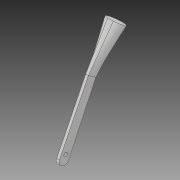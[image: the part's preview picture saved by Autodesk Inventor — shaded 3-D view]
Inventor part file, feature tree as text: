
AUTODESK INVENTOR PART (.ipt)
format: ipt  version: 2017 (Build 210142000, 142)  size: 156,160 bytes
history: native  units: mm
features: thicken_offset x4, sketch x3, extrude x1, fillet x1, plane x1, loft x1, other x1
ambient origin geometry x8: Origin, YZ Plane, XZ Plane, XY Plane, X Axis, Y Axis, Z Axis, Center Point
bodies: Solid1 (feature_tree)
feature tree (12):
  extrude  "Extrusion1"  Depth=10.0mm TaperAngle=0.0deg
  fillet  "Fillet1"  Radius=15.0mm
  thicken_offset  "Thicken1"
  thicken_offset  "Thicken2"
  thicken_offset  "Thicken3"
  sketch  "Sketch2"  dims[d4=50.0mm d5=50.0mm]
  plane  "Work Plane1"
  loft  "Loft1"
  thicken_offset  "Thicken4"
  sketch  "Sketch1"  dims[d0=14.0mm d1=10.0mm d2=0.0mm d3=15.0mm]
  sketch  "Sketch3"  dims[d6=50.0mm d7=50.0mm d8=50.0mm d9=50.0mm d10=120.0mm d11=50.0mm d12=0.0mm d13=90.0deg d14=0.0mm d15=90.0deg d16=40.0mm d17=40.0mm]
  other  "Edges1"
